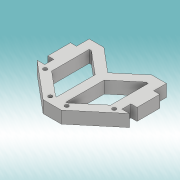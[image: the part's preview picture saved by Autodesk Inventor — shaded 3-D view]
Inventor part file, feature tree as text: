
AUTODESK INVENTOR PART (.ipt)
format: ipt  version: 2019 (Build 230136000, 136)  size: 154,624 bytes
history: native  units: mm
features: extrude x1
ambient origin geometry x8: Origin, YZ Plane, XZ Plane, XY Plane, X Axis, Y Axis, Z Axis, Center Point
bodies: Solid1 (feature_tree)
feature tree (1):
  extrude  "Extrusion1"  Depth=5.0135mm
